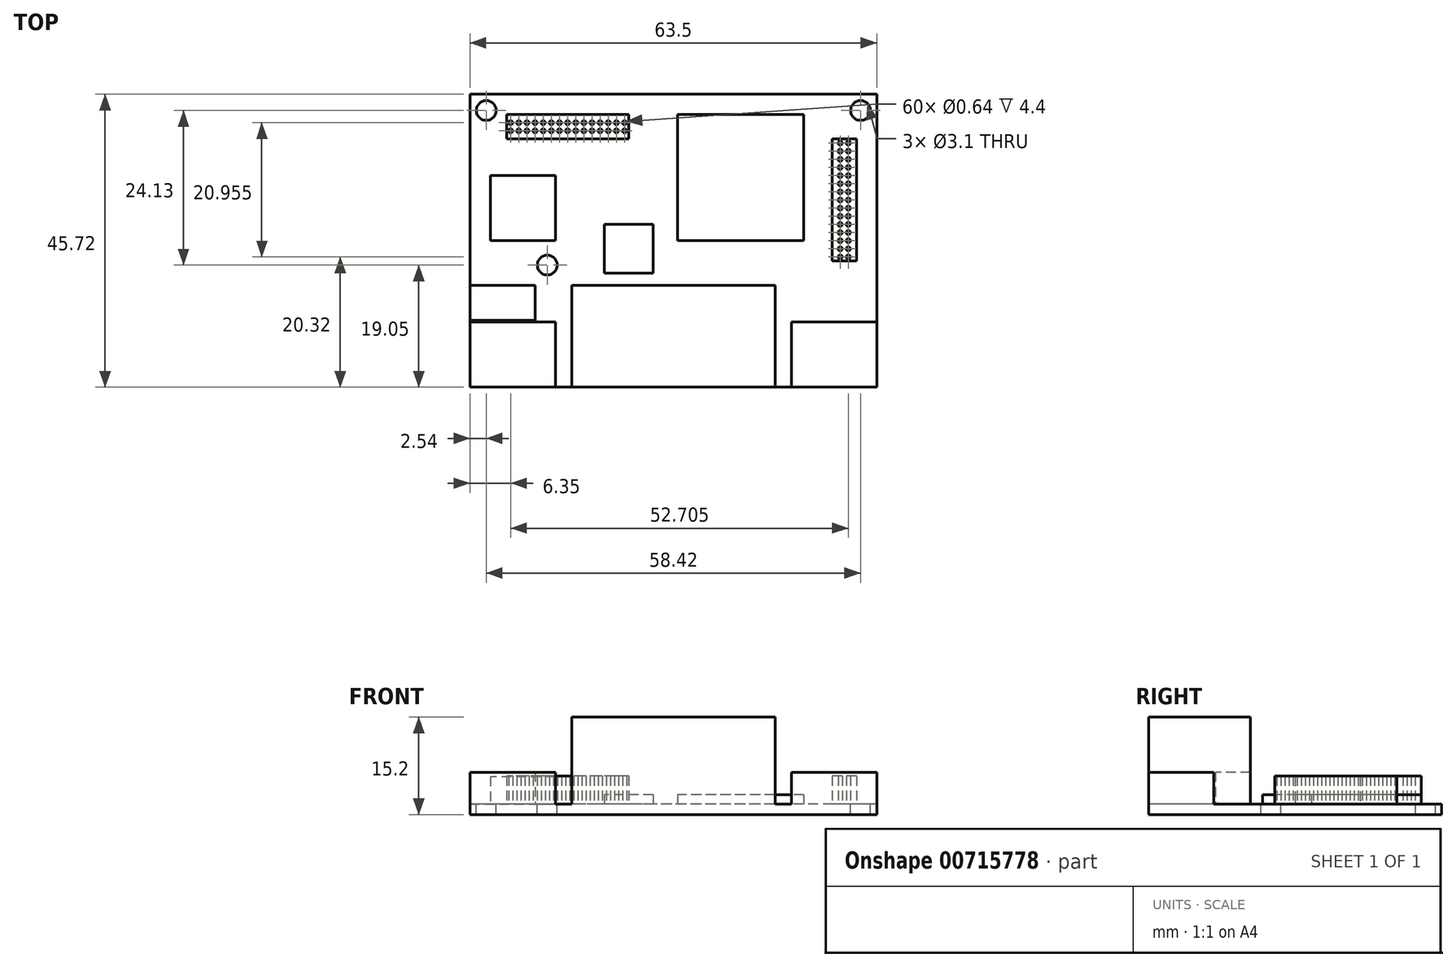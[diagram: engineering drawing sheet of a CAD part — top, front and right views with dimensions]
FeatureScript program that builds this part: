
annotation { "Feature Type Name" : "Feature", "Feature Type Description" : "" }
export const myFeature = defineFeature(function(context is Context, id is Id, definition is map)
    precondition{}
    {
        {
            var Q0;
            Q0=qCreatedBy(makeId("Top.planeOp"),FACE);
            var sketch = newSketch(context, id + "F0", { "sketchPlane" : qUnion([Q0])});
            skLineSegment(sketch, "E0.bottom", {"start": v(31.75, 22.86) * mm, "end": v(-31.75, 22.86) * mm});
            skLineSegment(sketch, "E0.top", {"start": v(31.75, -22.86) * mm, "end": v(-31.75, -22.86) * mm});
            skLineSegment(sketch, "E0.left", {"start": v(31.75, 22.86) * mm, "end": v(31.75, -22.86) * mm});
            skLineSegment(sketch, "E0.right", {"start": v(-31.75, 22.86) * mm, "end": v(-31.75, -22.86) * mm});
            skPoint(sketch, "E0.middle", {"position": v(0, 0) * mm});
            skCircle(sketch, "E1", {"center": v(-29.21, 20.32) * mm, "radius": 1.55 * mm});
            skCircle(sketch, "E2", {"center": v(29.21, 20.32) * mm, "radius": 1.55 * mm});
            skCircle(sketch, "E3", {"center": v(-19.69, -3.81) * mm, "radius": 1.55 * mm});
            skLineSegment(sketch, "E4.bottom", {"start": v(-18.41, 10.16) * mm, "end": v(-28.57, 10.16) * mm});
            skLineSegment(sketch, "E4.top", {"start": v(-18.41, 0) * mm, "end": v(-28.57, 0) * mm});
            skLineSegment(sketch, "E4.left", {"start": v(-18.41, 10.16) * mm, "end": v(-18.41, 0) * mm});
            skLineSegment(sketch, "E4.right", {"start": v(-28.57, 10.16) * mm, "end": v(-28.57, 0) * mm});
            skPoint(sketch, "E4.middle", {"position": v(-23.5, 5.08) * mm});
            skLineSegment(sketch, "E5.bottom", {"start": v(20.32, 19.69) * mm, "end": v(0.63, 19.69) * mm});
            skLineSegment(sketch, "E5.top", {"start": v(20.32, 0) * mm, "end": v(0.63, 0) * mm});
            skLineSegment(sketch, "E5.left", {"start": v(20.32, 19.69) * mm, "end": v(20.32, 0) * mm});
            skLineSegment(sketch, "E5.right", {"start": v(0.64, 19.69) * mm, "end": v(0.64, 0) * mm});
            skPoint(sketch, "E5.middle", {"position": v(10.48, 9.84) * mm});
            skLineSegment(sketch, "E6.bottom", {"start": v(-3.17, 2.54) * mm, "end": v(-10.8, 2.54) * mm});
            skLineSegment(sketch, "E6.top", {"start": v(-3.17, -5.08) * mm, "end": v(-10.8, -5.08) * mm});
            skLineSegment(sketch, "E6.left", {"start": v(-3.17, 2.54) * mm, "end": v(-3.17, -5.08) * mm});
            skLineSegment(sketch, "E6.right", {"start": v(-10.8, 2.54) * mm, "end": v(-10.8, -5.08) * mm});
            skPoint(sketch, "E6.middle", {"position": v(-6.98, -1.27) * mm});
            skLineSegment(sketch, "E7.bottom", {"start": v(-31.75, -22.86) * mm, "end": v(-18.41, -22.86) * mm});
            skLineSegment(sketch, "E7.top", {"start": v(-31.75, -12.7) * mm, "end": v(-18.42, -12.7) * mm});
            skLineSegment(sketch, "E7.left", {"start": v(-31.75, -22.86) * mm, "end": v(-31.75, -12.7) * mm});
            skLineSegment(sketch, "E7.right", {"start": v(-18.41, -22.86) * mm, "end": v(-18.41, -12.7) * mm});
            skPoint(sketch, "E7.middle", {"position": v(-25.08, -17.78) * mm});
            skLineSegment(sketch, "E8.bottom", {"start": v(-21.6, -6.99) * mm, "end": v(-31.75, -6.99) * mm});
            skLineSegment(sketch, "E8.top", {"start": v(-21.59, -12.45) * mm, "end": v(-31.75, -12.45) * mm});
            skLineSegment(sketch, "E8.left", {"start": v(-21.59, -6.99) * mm, "end": v(-21.59, -12.45) * mm});
            skLineSegment(sketch, "E8.right", {"start": v(-31.75, -6.99) * mm, "end": v(-31.75, -12.45) * mm});
            skPoint(sketch, "E8.middle", {"position": v(-26.67, -9.72) * mm});
            skLineSegment(sketch, "E9.bottom", {"start": v(31.75, -12.7) * mm, "end": v(18.41, -12.7) * mm});
            skLineSegment(sketch, "E9.top", {"start": v(31.75, -22.86) * mm, "end": v(18.41, -22.86) * mm});
            skLineSegment(sketch, "E9.left", {"start": v(31.75, -12.7) * mm, "end": v(31.75, -22.86) * mm});
            skLineSegment(sketch, "E9.right", {"start": v(18.41, -12.7) * mm, "end": v(18.41, -22.86) * mm});
            skPoint(sketch, "E9.middle", {"position": v(25.08, -17.78) * mm});
            skLineSegment(sketch, "E10.bottom", {"start": v(15.88, -6.99) * mm, "end": v(-15.88, -6.99) * mm});
            skLineSegment(sketch, "E10.top", {"start": v(15.88, -22.86) * mm, "end": v(-15.88, -22.86) * mm});
            skLineSegment(sketch, "E10.left", {"start": v(15.88, -6.99) * mm, "end": v(15.88, -22.86) * mm});
            skLineSegment(sketch, "E10.right", {"start": v(-15.88, -6.99) * mm, "end": v(-15.88, -22.86) * mm});
            skPoint(sketch, "E10.middle", {"position": v(0, -14.92) * mm});
            skCircle(sketch, "E11", {"center": v(-25.4, 18.41) * mm, "radius": 0.32 * mm});
            skCircle(sketch, "E12.1.0.0", {"center": v(-24.13, 18.41) * mm, "radius": 0.32 * mm});
            skCircle(sketch, "E12.2.0.0", {"center": v(-22.86, 18.41) * mm, "radius": 0.32 * mm});
            skCircle(sketch, "E12.3.0.0", {"center": v(-21.59, 18.41) * mm, "radius": 0.32 * mm});
            skCircle(sketch, "E12.4.0.0", {"center": v(-20.32, 18.41) * mm, "radius": 0.32 * mm});
            skCircle(sketch, "E12.5.0.0", {"center": v(-19.05, 18.41) * mm, "radius": 0.32 * mm});
            skCircle(sketch, "E12.6.0.0", {"center": v(-17.78, 18.41) * mm, "radius": 0.32 * mm});
            skCircle(sketch, "E12.7.0.0", {"center": v(-16.51, 18.41) * mm, "radius": 0.32 * mm});
            skCircle(sketch, "E12.8.0.0", {"center": v(-15.24, 18.41) * mm, "radius": 0.32 * mm});
            skCircle(sketch, "E12.9.0.0", {"center": v(-13.97, 18.41) * mm, "radius": 0.32 * mm});
            skCircle(sketch, "E12.10.0.0", {"center": v(-12.7, 18.41) * mm, "radius": 0.32 * mm});
            skCircle(sketch, "E12.11.0.0", {"center": v(-11.43, 18.41) * mm, "radius": 0.32 * mm});
            skCircle(sketch, "E12.12.0.0", {"center": v(-10.16, 18.41) * mm, "radius": 0.32 * mm});
            skCircle(sketch, "E12.13.0.0", {"center": v(-8.89, 18.41) * mm, "radius": 0.32 * mm});
            skCircle(sketch, "E12.14.0.0", {"center": v(-7.62, 18.41) * mm, "radius": 0.32 * mm});
            skLineSegment(sketch, "E12.direction1", {"start": v(-25.4, 18.41) * mm, "end": v(-24.13, 18.41) * mm, "construction": true});
            skCircle(sketch, "E13.1.0.0", {"center": v(-19.05, 17.14) * mm, "radius": 0.32 * mm});
            skCircle(sketch, "E13.1.0.1", {"center": v(-17.78, 17.14) * mm, "radius": 0.32 * mm});
            skCircle(sketch, "E13.1.0.2", {"center": v(-16.51, 17.14) * mm, "radius": 0.32 * mm});
            skCircle(sketch, "E13.1.0.3", {"center": v(-13.97, 17.14) * mm, "radius": 0.32 * mm});
            skCircle(sketch, "E13.1.0.4", {"center": v(-11.43, 17.14) * mm, "radius": 0.32 * mm});
            skCircle(sketch, "E13.1.0.5", {"center": v(-8.89, 17.14) * mm, "radius": 0.32 * mm});
            skCircle(sketch, "E13.1.0.6", {"center": v(-25.4, 17.15) * mm, "radius": 0.32 * mm});
            skCircle(sketch, "E13.1.0.7", {"center": v(-24.13, 17.15) * mm, "radius": 0.32 * mm});
            skCircle(sketch, "E13.1.0.8", {"center": v(-22.86, 17.14) * mm, "radius": 0.32 * mm});
            skCircle(sketch, "E13.1.0.9", {"center": v(-21.59, 17.14) * mm, "radius": 0.32 * mm});
            skCircle(sketch, "E13.1.0.10", {"center": v(-20.32, 17.14) * mm, "radius": 0.32 * mm});
            skLineSegment(sketch, "E13.1.0.11", {"start": v(-25.4, 17.14) * mm, "end": v(-24.13, 17.14) * mm, "construction": true});
            skCircle(sketch, "E13.1.0.12", {"center": v(-7.62, 17.14) * mm, "radius": 0.32 * mm});
            skCircle(sketch, "E13.1.0.13", {"center": v(-10.16, 17.14) * mm, "radius": 0.32 * mm});
            skCircle(sketch, "E13.1.0.14", {"center": v(-12.7, 17.14) * mm, "radius": 0.32 * mm});
            skCircle(sketch, "E13.1.0.15", {"center": v(-15.24, 17.14) * mm, "radius": 0.32 * mm});
            skLineSegment(sketch, "E13.direction1", {"start": v(-25.4, 18.41) * mm, "end": v(-25.4, 17.15) * mm, "construction": true});
            skCircle(sketch, "E14", {"center": v(26.04, -2.54) * mm, "radius": 0.32 * mm});
            skCircle(sketch, "E15.1.0.0", {"center": v(26.03, -1.27) * mm, "radius": 0.32 * mm});
            skCircle(sketch, "E15.2.0.0", {"center": v(26.04, 0) * mm, "radius": 0.32 * mm});
            skCircle(sketch, "E15.3.0.0", {"center": v(26.04, 1.27) * mm, "radius": 0.32 * mm});
            skCircle(sketch, "E15.4.0.0", {"center": v(26.04, 2.54) * mm, "radius": 0.32 * mm});
            skCircle(sketch, "E15.5.0.0", {"center": v(26.04, 3.8) * mm, "radius": 0.32 * mm});
            skCircle(sketch, "E15.6.0.0", {"center": v(26.04, 5.08) * mm, "radius": 0.32 * mm});
            skCircle(sketch, "E15.7.0.0", {"center": v(26.04, 6.35) * mm, "radius": 0.32 * mm});
            skCircle(sketch, "E15.8.0.0", {"center": v(26.04, 7.62) * mm, "radius": 0.32 * mm});
            skCircle(sketch, "E15.9.0.0", {"center": v(26.04, 8.89) * mm, "radius": 0.32 * mm});
            skCircle(sketch, "E15.10.0.0", {"center": v(26.04, 10.16) * mm, "radius": 0.32 * mm});
            skCircle(sketch, "E15.11.0.0", {"center": v(26.04, 11.43) * mm, "radius": 0.32 * mm});
            skCircle(sketch, "E15.12.0.0", {"center": v(26.04, 12.7) * mm, "radius": 0.32 * mm});
            skCircle(sketch, "E15.13.0.0", {"center": v(26.04, 13.97) * mm, "radius": 0.32 * mm});
            skCircle(sketch, "E15.14.0.0", {"center": v(26.04, 15.24) * mm, "radius": 0.32 * mm});
            skLineSegment(sketch, "E15.direction1", {"start": v(26.04, -2.54) * mm, "end": v(26.04, -1.27) * mm, "construction": true});
            skCircle(sketch, "E16.1.0.0", {"center": v(27.3, 3.8) * mm, "radius": 0.32 * mm});
            skCircle(sketch, "E16.1.0.1", {"center": v(27.3, 5.08) * mm, "radius": 0.32 * mm});
            skCircle(sketch, "E16.1.0.2", {"center": v(27.3, 6.35) * mm, "radius": 0.32 * mm});
            skCircle(sketch, "E16.1.0.3", {"center": v(27.3, 8.89) * mm, "radius": 0.32 * mm});
            skCircle(sketch, "E16.1.0.4", {"center": v(27.3, 11.43) * mm, "radius": 0.32 * mm});
            skCircle(sketch, "E16.1.0.5", {"center": v(27.3, 13.97) * mm, "radius": 0.32 * mm});
            skCircle(sketch, "E16.1.0.6", {"center": v(27.3, -2.54) * mm, "radius": 0.32 * mm});
            skCircle(sketch, "E16.1.0.7", {"center": v(27.3, -1.27) * mm, "radius": 0.32 * mm});
            skCircle(sketch, "E16.1.0.8", {"center": v(27.3, 0) * mm, "radius": 0.32 * mm});
            skCircle(sketch, "E16.1.0.9", {"center": v(27.3, 1.27) * mm, "radius": 0.32 * mm});
            skCircle(sketch, "E16.1.0.10", {"center": v(27.3, 2.54) * mm, "radius": 0.32 * mm});
            skLineSegment(sketch, "E16.1.0.11", {"start": v(27.3, -2.54) * mm, "end": v(27.3, -1.27) * mm, "construction": true});
            skCircle(sketch, "E16.1.0.12", {"center": v(27.3, 15.24) * mm, "radius": 0.32 * mm});
            skCircle(sketch, "E16.1.0.13", {"center": v(27.3, 12.7) * mm, "radius": 0.32 * mm});
            skCircle(sketch, "E16.1.0.14", {"center": v(27.3, 10.16) * mm, "radius": 0.32 * mm});
            skCircle(sketch, "E16.1.0.15", {"center": v(27.3, 7.62) * mm, "radius": 0.32 * mm});
            skLineSegment(sketch, "E16.direction1", {"start": v(26.04, -2.54) * mm, "end": v(27.3, -2.54) * mm, "construction": true});
            skLineSegment(sketch, "E17.bottom", {"start": v(-6.98, 19.69) * mm, "end": v(-26.04, 19.69) * mm});
            skLineSegment(sketch, "E17.top", {"start": v(-6.98, 15.87) * mm, "end": v(-26.04, 15.87) * mm});
            skLineSegment(sketch, "E17.left", {"start": v(-6.98, 19.69) * mm, "end": v(-6.98, 15.87) * mm});
            skLineSegment(sketch, "E17.right", {"start": v(-26.04, 19.69) * mm, "end": v(-26.04, 15.87) * mm});
            skPoint(sketch, "E17.middle", {"position": v(-16.5, 17.78) * mm});
            skLineSegment(sketch, "E18.bottom", {"start": v(28.58, 15.87) * mm, "end": v(24.77, 15.87) * mm});
            skLineSegment(sketch, "E18.top", {"start": v(28.58, -3.18) * mm, "end": v(24.77, -3.18) * mm});
            skLineSegment(sketch, "E18.left", {"start": v(28.58, 15.87) * mm, "end": v(28.58, -3.18) * mm});
            skLineSegment(sketch, "E18.right", {"start": v(24.77, 15.87) * mm, "end": v(24.77, -3.18) * mm});
            skPoint(sketch, "E18.middle", {"position": v(26.67, 6.35) * mm});
            skSolve(sketch);
        }
        {
            var Q0;
            Q0=makeQuery(id+"F0.imprint","IMPRINT",FACE,{"disambiguationData":[TD([[makeQuery(id+"F0.imprint","IMPRINT",EDGE,{"derivedFrom":sQuery(id+"F0.wireOp",EDGE,"E14")}),-1.0]])]});
            var Q1;
            Q1=makeQuery(id+"F0.imprint","IMPRINT",FACE,{"disambiguationData":[TD([[makeQuery(id+"F0.imprint","IMPRINT",EDGE,{"derivedFrom":sQuery(id+"F0.wireOp",EDGE,"E4.bottom")}),1.0]])]});
            var Q2;
            Q2=makeQuery(id+"F0.imprint","IMPRINT",FACE,{"disambiguationData":[TD([[makeQuery(id+"F0.imprint","IMPRINT",EDGE,{"derivedFrom":sQuery(id+"F0.wireOp",EDGE,"E5.bottom")}),1.0]])]});
            var Q3;
            {var subQ0=sQuery(id+"F0.wireOp",EDGE,"E8.bottom");Q3=makeQuery(id+"F0.imprint","IMPRINT",FACE,{"disambiguationData":[TD([[makeQuery(id+"F0.imprint","IMPRINT",EDGE,{"derivedFrom":subQ0}),1.0]])]});}
            var Q4;
            {var subQ4=sQuery(id+"F0.wireOp",EDGE,"E7.top");Q4=makeQuery(id+"F0.imprint","IMPRINT",FACE,{"disambiguationData":[TD([[makeQuery(id+"F0.imprint","IMPRINT",EDGE,{"derivedFrom":subQ4}),-1.0]])]});}
            var Q5;
            Q5=makeQuery(id+"F0.imprint","IMPRINT",FACE,{"disambiguationData":[TD([[makeQuery(id+"F0.imprint","IMPRINT",EDGE,{"derivedFrom":sQuery(id+"F0.wireOp",EDGE,"E11")}),-1.0]])]});
            var Q6;
            {var subQ1=sQuery(id+"F0.wireOp",EDGE,"E0.bottom");Q6=makeQuery(id+"F0.imprint","IMPRINT",FACE,{"disambiguationData":[TD([[makeQuery(id+"F0.imprint","IMPRINT",EDGE,{"derivedFrom":subQ1}),1.0]])]});}
            var Q7;
            Q7=makeQuery(id+"F0.imprint","IMPRINT",FACE,{"disambiguationData":[TD([[makeQuery(id+"F0.imprint","IMPRINT",EDGE,{"derivedFrom":sQuery(id+"F0.wireOp",EDGE,"E6.bottom")}),1.0]])]});
            var Q8;
            Q8=makeQuery(id+"F0.imprint","IMPRINT",FACE,{"disambiguationData":[TD([[makeQuery(id+"F0.imprint","IMPRINT",EDGE,{"derivedFrom":sQuery(id+"F0.wireOp",EDGE,"E10.bottom")}),1.0]])]});
            var Q9;
            {var subQ4=sQuery(id+"F0.wireOp",EDGE,"E9.bottom");Q9=makeQuery(id+"F0.imprint","IMPRINT",FACE,{"disambiguationData":[TD([[makeQuery(id+"F0.imprint","IMPRINT",EDGE,{"derivedFrom":subQ4}),1.0]])]});}
            var Q10;
            Q10=makeQuery(id+"F0.imprint","IMPRINT",FACE,{"disambiguationData":[TD([[makeQuery(id+"F0.imprint","IMPRINT",EDGE,{"derivedFrom":sQuery(id+"F0.wireOp",EDGE,"E16.1.0.4")}),1.0]])]});
            var Q11;
            Q11=makeQuery(id+"F0.imprint","IMPRINT",FACE,{"disambiguationData":[TD([[makeQuery(id+"F0.imprint","IMPRINT",EDGE,{"derivedFrom":sQuery(id+"F0.wireOp",EDGE,"E16.1.0.1")}),1.0]])]});
            var Q12;
            Q12=makeQuery(id+"F0.imprint","IMPRINT",FACE,{"disambiguationData":[TD([[makeQuery(id+"F0.imprint","IMPRINT",EDGE,{"derivedFrom":sQuery(id+"F0.wireOp",EDGE,"E15.8.0.0")}),1.0]])]});
            var Q13;
            Q13=makeQuery(id+"F0.imprint","IMPRINT",FACE,{"disambiguationData":[TD([[makeQuery(id+"F0.imprint","IMPRINT",EDGE,{"derivedFrom":sQuery(id+"F0.wireOp",EDGE,"E15.11.0.0")}),1.0]])]});
            var Q14;
            Q14=makeQuery(id+"F0.imprint","IMPRINT",FACE,{"disambiguationData":[TD([[makeQuery(id+"F0.imprint","IMPRINT",EDGE,{"derivedFrom":sQuery(id+"F0.wireOp",EDGE,"E12.10.0.0")}),1.0]])]});
            var Q15;
            Q15=makeQuery(id+"F0.imprint","IMPRINT",FACE,{"disambiguationData":[TD([[makeQuery(id+"F0.imprint","IMPRINT",EDGE,{"derivedFrom":sQuery(id+"F0.wireOp",EDGE,"E13.1.0.8")}),1.0]])]});
            var Q16;
            Q16=makeQuery(id+"F0.imprint","IMPRINT",FACE,{"disambiguationData":[TD([[makeQuery(id+"F0.imprint","IMPRINT",EDGE,{"derivedFrom":sQuery(id+"F0.wireOp",EDGE,"E15.7.0.0")}),1.0]])]});
            var Q17;
            Q17=makeQuery(id+"F0.imprint","IMPRINT",FACE,{"disambiguationData":[TD([[makeQuery(id+"F0.imprint","IMPRINT",EDGE,{"derivedFrom":sQuery(id+"F0.wireOp",EDGE,"E12.14.0.0")}),1.0]])]});
            var Q18;
            Q18=makeQuery(id+"F0.imprint","IMPRINT",FACE,{"disambiguationData":[TD([[makeQuery(id+"F0.imprint","IMPRINT",EDGE,{"derivedFrom":sQuery(id+"F0.wireOp",EDGE,"E15.6.0.0")}),1.0]])]});
            var Q19;
            Q19=makeQuery(id+"F0.imprint","IMPRINT",FACE,{"disambiguationData":[TD([[makeQuery(id+"F0.imprint","IMPRINT",EDGE,{"derivedFrom":sQuery(id+"F0.wireOp",EDGE,"E12.12.0.0")}),1.0]])]});
            var Q20;
            Q20=makeQuery(id+"F0.imprint","IMPRINT",FACE,{"disambiguationData":[TD([[makeQuery(id+"F0.imprint","IMPRINT",EDGE,{"derivedFrom":sQuery(id+"F0.wireOp",EDGE,"E13.1.0.1")}),1.0]])]});
            var Q21;
            Q21=makeQuery(id+"F0.imprint","IMPRINT",FACE,{"disambiguationData":[TD([[makeQuery(id+"F0.imprint","IMPRINT",EDGE,{"derivedFrom":sQuery(id+"F0.wireOp",EDGE,"E12.3.0.0")}),1.0]])]});
            var Q22;
            Q22=makeQuery(id+"F0.imprint","IMPRINT",FACE,{"disambiguationData":[TD([[makeQuery(id+"F0.imprint","IMPRINT",EDGE,{"derivedFrom":sQuery(id+"F0.wireOp",EDGE,"E13.1.0.12")}),1.0]])]});
            var Q23;
            Q23=makeQuery(id+"F0.imprint","IMPRINT",FACE,{"disambiguationData":[TD([[makeQuery(id+"F0.imprint","IMPRINT",EDGE,{"derivedFrom":sQuery(id+"F0.wireOp",EDGE,"E13.1.0.2")}),1.0]])]});
            var Q24;
            Q24=makeQuery(id+"F0.imprint","IMPRINT",FACE,{"disambiguationData":[TD([[makeQuery(id+"F0.imprint","IMPRINT",EDGE,{"derivedFrom":sQuery(id+"F0.wireOp",EDGE,"E12.13.0.0")}),1.0]])]});
            var Q25;
            Q25=makeQuery(id+"F0.imprint","IMPRINT",FACE,{"disambiguationData":[TD([[makeQuery(id+"F0.imprint","IMPRINT",EDGE,{"derivedFrom":sQuery(id+"F0.wireOp",EDGE,"E15.2.0.0")}),1.0]])]});
            var Q26;
            Q26=makeQuery(id+"F0.imprint","IMPRINT",FACE,{"disambiguationData":[TD([[makeQuery(id+"F0.imprint","IMPRINT",EDGE,{"derivedFrom":sQuery(id+"F0.wireOp",EDGE,"E16.1.0.13")}),1.0]])]});
            var Q27;
            Q27=makeQuery(id+"F0.imprint","IMPRINT",FACE,{"disambiguationData":[TD([[makeQuery(id+"F0.imprint","IMPRINT",EDGE,{"derivedFrom":sQuery(id+"F0.wireOp",EDGE,"E13.1.0.0")}),1.0]])]});
            var Q28;
            Q28=makeQuery(id+"F0.imprint","IMPRINT",FACE,{"disambiguationData":[TD([[makeQuery(id+"F0.imprint","IMPRINT",EDGE,{"derivedFrom":sQuery(id+"F0.wireOp",EDGE,"E16.1.0.14")}),1.0]])]});
            var Q29;
            Q29=makeQuery(id+"F0.imprint","IMPRINT",FACE,{"disambiguationData":[TD([[makeQuery(id+"F0.imprint","IMPRINT",EDGE,{"derivedFrom":sQuery(id+"F0.wireOp",EDGE,"E15.12.0.0")}),1.0]])]});
            var Q30;
            Q30=makeQuery(id+"F0.imprint","IMPRINT",FACE,{"disambiguationData":[TD([[makeQuery(id+"F0.imprint","IMPRINT",EDGE,{"derivedFrom":sQuery(id+"F0.wireOp",EDGE,"E15.3.0.0")}),1.0]])]});
            var Q31;
            Q31=makeQuery(id+"F0.imprint","IMPRINT",FACE,{"disambiguationData":[TD([[makeQuery(id+"F0.imprint","IMPRINT",EDGE,{"derivedFrom":sQuery(id+"F0.wireOp",EDGE,"E12.11.0.0")}),1.0]])]});
            var Q32;
            Q32=makeQuery(id+"F0.imprint","IMPRINT",FACE,{"disambiguationData":[TD([[makeQuery(id+"F0.imprint","IMPRINT",EDGE,{"derivedFrom":sQuery(id+"F0.wireOp",EDGE,"E15.13.0.0")}),1.0]])]});
            var Q33;
            Q33=makeQuery(id+"F0.imprint","IMPRINT",FACE,{"disambiguationData":[TD([[makeQuery(id+"F0.imprint","IMPRINT",EDGE,{"derivedFrom":sQuery(id+"F0.wireOp",EDGE,"E12.2.0.0")}),1.0]])]});
            var Q34;
            Q34=makeQuery(id+"F0.imprint","IMPRINT",FACE,{"disambiguationData":[TD([[makeQuery(id+"F0.imprint","IMPRINT",EDGE,{"derivedFrom":sQuery(id+"F0.wireOp",EDGE,"E15.10.0.0")}),1.0]])]});
            var Q35;
            Q35=makeQuery(id+"F0.imprint","IMPRINT",FACE,{"disambiguationData":[TD([[makeQuery(id+"F0.imprint","IMPRINT",EDGE,{"derivedFrom":sQuery(id+"F0.wireOp",EDGE,"E13.1.0.9")}),1.0]])]});
            var Q36;
            Q36=makeQuery(id+"F0.imprint","IMPRINT",FACE,{"disambiguationData":[TD([[makeQuery(id+"F0.imprint","IMPRINT",EDGE,{"derivedFrom":sQuery(id+"F0.wireOp",EDGE,"E16.1.0.9")}),1.0]])]});
            var Q37;
            Q37=makeQuery(id+"F0.imprint","IMPRINT",FACE,{"disambiguationData":[TD([[makeQuery(id+"F0.imprint","IMPRINT",EDGE,{"derivedFrom":sQuery(id+"F0.wireOp",EDGE,"E16.1.0.5")}),1.0]])]});
            var Q38;
            Q38=makeQuery(id+"F0.imprint","IMPRINT",FACE,{"disambiguationData":[TD([[makeQuery(id+"F0.imprint","IMPRINT",EDGE,{"derivedFrom":sQuery(id+"F0.wireOp",EDGE,"E12.6.0.0")}),1.0]])]});
            var Q39;
            Q39=makeQuery(id+"F0.imprint","IMPRINT",FACE,{"disambiguationData":[TD([[makeQuery(id+"F0.imprint","IMPRINT",EDGE,{"derivedFrom":sQuery(id+"F0.wireOp",EDGE,"E15.14.0.0")}),1.0]])]});
            var Q40;
            Q40=makeQuery(id+"F0.imprint","IMPRINT",FACE,{"disambiguationData":[TD([[makeQuery(id+"F0.imprint","IMPRINT",EDGE,{"derivedFrom":sQuery(id+"F0.wireOp",EDGE,"E16.1.0.8")}),1.0]])]});
            var Q41;
            Q41=makeQuery(id+"F0.imprint","IMPRINT",FACE,{"disambiguationData":[TD([[makeQuery(id+"F0.imprint","IMPRINT",EDGE,{"derivedFrom":sQuery(id+"F0.wireOp",EDGE,"E13.1.0.10")}),1.0]])]});
            var Q42;
            Q42=makeQuery(id+"F0.imprint","IMPRINT",FACE,{"disambiguationData":[TD([[makeQuery(id+"F0.imprint","IMPRINT",EDGE,{"derivedFrom":sQuery(id+"F0.wireOp",EDGE,"E12.5.0.0")}),1.0]])]});
            var Q43;
            Q43=makeQuery(id+"F0.imprint","IMPRINT",FACE,{"disambiguationData":[TD([[makeQuery(id+"F0.imprint","IMPRINT",EDGE,{"derivedFrom":sQuery(id+"F0.wireOp",EDGE,"E16.1.0.3")}),1.0]])]});
            var Q44;
            Q44=makeQuery(id+"F0.imprint","IMPRINT",FACE,{"disambiguationData":[TD([[makeQuery(id+"F0.imprint","IMPRINT",EDGE,{"derivedFrom":sQuery(id+"F0.wireOp",EDGE,"E15.5.0.0")}),1.0]])]});
            var Q45;
            Q45=makeQuery(id+"F0.imprint","IMPRINT",FACE,{"disambiguationData":[TD([[makeQuery(id+"F0.imprint","IMPRINT",EDGE,{"derivedFrom":sQuery(id+"F0.wireOp",EDGE,"E12.7.0.0")}),1.0]])]});
            var Q46;
            Q46=makeQuery(id+"F0.imprint","IMPRINT",FACE,{"disambiguationData":[TD([[makeQuery(id+"F0.imprint","IMPRINT",EDGE,{"derivedFrom":sQuery(id+"F0.wireOp",EDGE,"E15.9.0.0")}),1.0]])]});
            var Q47;
            Q47=makeQuery(id+"F0.imprint","IMPRINT",FACE,{"disambiguationData":[TD([[makeQuery(id+"F0.imprint","IMPRINT",EDGE,{"derivedFrom":sQuery(id+"F0.wireOp",EDGE,"E16.1.0.10")}),1.0]])]});
            var Q48;
            Q48=makeQuery(id+"F0.imprint","IMPRINT",FACE,{"disambiguationData":[TD([[makeQuery(id+"F0.imprint","IMPRINT",EDGE,{"derivedFrom":sQuery(id+"F0.wireOp",EDGE,"E13.1.0.5")}),1.0]])]});
            var Q49;
            Q49=makeQuery(id+"F0.imprint","IMPRINT",FACE,{"disambiguationData":[TD([[makeQuery(id+"F0.imprint","IMPRINT",EDGE,{"derivedFrom":sQuery(id+"F0.wireOp",EDGE,"E15.4.0.0")}),1.0]])]});
            var Q50;
            Q50=makeQuery(id+"F0.imprint","IMPRINT",FACE,{"disambiguationData":[TD([[makeQuery(id+"F0.imprint","IMPRINT",EDGE,{"derivedFrom":sQuery(id+"F0.wireOp",EDGE,"E13.1.0.13")}),1.0]])]});
            var Q51;
            Q51=makeQuery(id+"F0.imprint","IMPRINT",FACE,{"disambiguationData":[TD([[makeQuery(id+"F0.imprint","IMPRINT",EDGE,{"derivedFrom":sQuery(id+"F0.wireOp",EDGE,"E16.1.0.2")}),1.0]])]});
            var Q52;
            Q52=makeQuery(id+"F0.imprint","IMPRINT",FACE,{"disambiguationData":[TD([[makeQuery(id+"F0.imprint","IMPRINT",EDGE,{"derivedFrom":sQuery(id+"F0.wireOp",EDGE,"E13.1.0.15")}),1.0]])]});
            var Q53;
            Q53=makeQuery(id+"F0.imprint","IMPRINT",FACE,{"disambiguationData":[TD([[makeQuery(id+"F0.imprint","IMPRINT",EDGE,{"derivedFrom":sQuery(id+"F0.wireOp",EDGE,"E13.1.0.3")}),1.0]])]});
            var Q54;
            Q54=makeQuery(id+"F0.imprint","IMPRINT",FACE,{"disambiguationData":[TD([[makeQuery(id+"F0.imprint","IMPRINT",EDGE,{"derivedFrom":sQuery(id+"F0.wireOp",EDGE,"E16.1.0.15")}),1.0]])]});
            var Q55;
            Q55=makeQuery(id+"F0.imprint","IMPRINT",FACE,{"disambiguationData":[TD([[makeQuery(id+"F0.imprint","IMPRINT",EDGE,{"derivedFrom":sQuery(id+"F0.wireOp",EDGE,"E13.1.0.4")}),1.0]])]});
            var Q56;
            Q56=makeQuery(id+"F0.imprint","IMPRINT",FACE,{"disambiguationData":[TD([[makeQuery(id+"F0.imprint","IMPRINT",EDGE,{"derivedFrom":sQuery(id+"F0.wireOp",EDGE,"E12.9.0.0")}),1.0]])]});
            var Q57;
            Q57=makeQuery(id+"F0.imprint","IMPRINT",FACE,{"disambiguationData":[TD([[makeQuery(id+"F0.imprint","IMPRINT",EDGE,{"derivedFrom":sQuery(id+"F0.wireOp",EDGE,"E13.1.0.14")}),1.0]])]});
            var Q58;
            Q58=makeQuery(id+"F0.imprint","IMPRINT",FACE,{"disambiguationData":[TD([[makeQuery(id+"F0.imprint","IMPRINT",EDGE,{"derivedFrom":sQuery(id+"F0.wireOp",EDGE,"E12.4.0.0")}),1.0]])]});
            var Q59;
            Q59=makeQuery(id+"F0.imprint","IMPRINT",FACE,{"disambiguationData":[TD([[makeQuery(id+"F0.imprint","IMPRINT",EDGE,{"derivedFrom":sQuery(id+"F0.wireOp",EDGE,"E16.1.0.0")}),1.0]])]});
            var Q60;
            Q60=makeQuery(id+"F0.imprint","IMPRINT",FACE,{"disambiguationData":[TD([[makeQuery(id+"F0.imprint","IMPRINT",EDGE,{"derivedFrom":sQuery(id+"F0.wireOp",EDGE,"E12.8.0.0")}),1.0]])]});
            var Q61;
            Q61=makeQuery(id+"F0.imprint","IMPRINT",FACE,{"disambiguationData":[TD([[makeQuery(id+"F0.imprint","IMPRINT",EDGE,{"derivedFrom":sQuery(id+"F0.wireOp",EDGE,"E16.1.0.12")}),1.0]])]});
            var Q62;
            Q62=makeQuery(id+"F0.imprint","IMPRINT",FACE,{"disambiguationData":[TD([[makeQuery(id+"F0.imprint","IMPRINT",EDGE,{"derivedFrom":sQuery(id+"F0.wireOp",EDGE,"E15.1.0.0")}),1.0]])]});
            var Q63;
            Q63=makeQuery(id+"F0.imprint","IMPRINT",FACE,{"disambiguationData":[TD([[makeQuery(id+"F0.imprint","IMPRINT",EDGE,{"derivedFrom":sQuery(id+"F0.wireOp",EDGE,"E16.1.0.7")}),1.0]])]});
            var Q64;
            Q64=makeQuery(id+"F0.imprint","IMPRINT",FACE,{"disambiguationData":[TD([[makeQuery(id+"F0.imprint","IMPRINT",EDGE,{"derivedFrom":sQuery(id+"F0.wireOp",EDGE,"E13.1.0.7")}),1.0]])]});
            var Q65;
            Q65=makeQuery(id+"F0.imprint","IMPRINT",FACE,{"disambiguationData":[TD([[makeQuery(id+"F0.imprint","IMPRINT",EDGE,{"derivedFrom":sQuery(id+"F0.wireOp",EDGE,"E12.1.0.0")}),1.0]])]});
            var Q66;
            Q66=makeQuery(id+"F0.imprint","IMPRINT",FACE,{"disambiguationData":[TD([[makeQuery(id+"F0.imprint","IMPRINT",EDGE,{"derivedFrom":sQuery(id+"F0.wireOp",EDGE,"E13.1.0.6")}),1.0]])]});
            var Q67;
            Q67=makeQuery(id+"F0.imprint","IMPRINT",FACE,{"disambiguationData":[TD([[makeQuery(id+"F0.imprint","IMPRINT",EDGE,{"derivedFrom":sQuery(id+"F0.wireOp",EDGE,"E14")}),1.0]])]});
            var Q68;
            Q68=makeQuery(id+"F0.imprint","IMPRINT",FACE,{"disambiguationData":[TD([[makeQuery(id+"F0.imprint","IMPRINT",EDGE,{"derivedFrom":sQuery(id+"F0.wireOp",EDGE,"E11")}),1.0]])]});
            var Q69;
            Q69=makeQuery(id+"F0.imprint","IMPRINT",FACE,{"disambiguationData":[TD([[makeQuery(id+"F0.imprint","IMPRINT",EDGE,{"derivedFrom":sQuery(id+"F0.wireOp",EDGE,"E16.1.0.6")}),1.0]])]});
            extrude(context, id + "F1", {"entities" : qUnion([Q0, Q1, Q2, Q3, Q4, Q5, Q6, Q7, Q8, Q9, Q10, Q11, Q12, Q13, Q14, Q15, Q16, Q17, Q18, Q19, Q20, Q21, Q22, Q23, Q24, Q25, Q26, Q27, Q28, Q29, Q30, Q31, Q32, Q33, Q34, Q35, Q36, Q37, Q38, Q39, Q40, Q41, Q42, Q43, Q44, Q45, Q46, Q47, Q48, Q49, Q50, Q51, Q52, Q53, Q54, Q55, Q56, Q57, Q58, Q59, Q60, Q61, Q62, Q63, Q64, Q65, Q66, Q67, Q68, Q69]), "oppositeDirection" : true, "depth" : 1.6 * mm});
        }
        {
            var Q0;
            Q0=makeQuery(id+"F0.imprint","IMPRINT",FACE,{"disambiguationData":[TD([[makeQuery(id+"F0.imprint","IMPRINT",EDGE,{"derivedFrom":sQuery(id+"F0.wireOp",EDGE,"E11")}),-1.0]])]});
            var Q1;
            Q1=makeQuery(id+"F0.imprint","IMPRINT",FACE,{"disambiguationData":[TD([[makeQuery(id+"F0.imprint","IMPRINT",EDGE,{"derivedFrom":sQuery(id+"F0.wireOp",EDGE,"E14")}),-1.0]])]});
            extrude(context, id + "F2", {"entities" : qUnion([Q0, Q1]), "operationType" : NewBodyOperationType.ADD, "depth" : 4.4 * mm});
        }
        {
            var Q0;
            Q0=makeQuery(id+"F0.imprint","IMPRINT",FACE,{"disambiguationData":[TD([[makeQuery(id+"F0.imprint","IMPRINT",EDGE,{"derivedFrom":sQuery(id+"F0.wireOp",EDGE,"E5.bottom")}),1.0]])]});
            var Q1;
            Q1=makeQuery(id+"F0.imprint","IMPRINT",FACE,{"disambiguationData":[TD([[makeQuery(id+"F0.imprint","IMPRINT",EDGE,{"derivedFrom":sQuery(id+"F0.wireOp",EDGE,"E6.bottom")}),1.0]])]});
            extrude(context, id + "F3", {"entities" : qUnion([Q0, Q1]), "operationType" : NewBodyOperationType.ADD, "depth" : 1.5 * mm});
        }
        {
            var Q0;
            Q0=makeQuery(id+"F0.imprint","IMPRINT",FACE,{"disambiguationData":[TD([[makeQuery(id+"F0.imprint","IMPRINT",EDGE,{"derivedFrom":sQuery(id+"F0.wireOp",EDGE,"E4.bottom")}),1.0]])]});
            extrude(context, id + "F4", {"entities" : qUnion([Q0]), "operationType" : NewBodyOperationType.ADD, "depth" : 4.3 * mm});
        }
        {
            var Q0;
            {var subQ0=sQuery(id+"F0.wireOp",EDGE,"E8.bottom");Q0=makeQuery(id+"F0.imprint","IMPRINT",FACE,{"disambiguationData":[TD([[makeQuery(id+"F0.imprint","IMPRINT",EDGE,{"derivedFrom":subQ0}),1.0]])]});}
            var Q1;
            {var subQ4=sQuery(id+"F0.wireOp",EDGE,"E7.top");Q1=makeQuery(id+"F0.imprint","IMPRINT",FACE,{"disambiguationData":[TD([[makeQuery(id+"F0.imprint","IMPRINT",EDGE,{"derivedFrom":subQ4}),-1.0]])]});}
            var Q2;
            {var subQ4=sQuery(id+"F0.wireOp",EDGE,"E9.bottom");Q2=makeQuery(id+"F0.imprint","IMPRINT",FACE,{"disambiguationData":[TD([[makeQuery(id+"F0.imprint","IMPRINT",EDGE,{"derivedFrom":subQ4}),1.0]])]});}
            extrude(context, id + "F5", {"entities" : qUnion([Q0, Q1, Q2]), "operationType" : NewBodyOperationType.ADD, "depth" : 5 * mm});
        }
        {
            var Q0;
            Q0=makeQuery(id+"F0.imprint","IMPRINT",FACE,{"disambiguationData":[TD([[makeQuery(id+"F0.imprint","IMPRINT",EDGE,{"derivedFrom":sQuery(id+"F0.wireOp",EDGE,"E10.bottom")}),1.0]])]});
            extrude(context, id + "F6", {"entities" : qUnion([Q0]), "operationType" : NewBodyOperationType.ADD, "depth" : 13.6 * mm});
        }
    });
